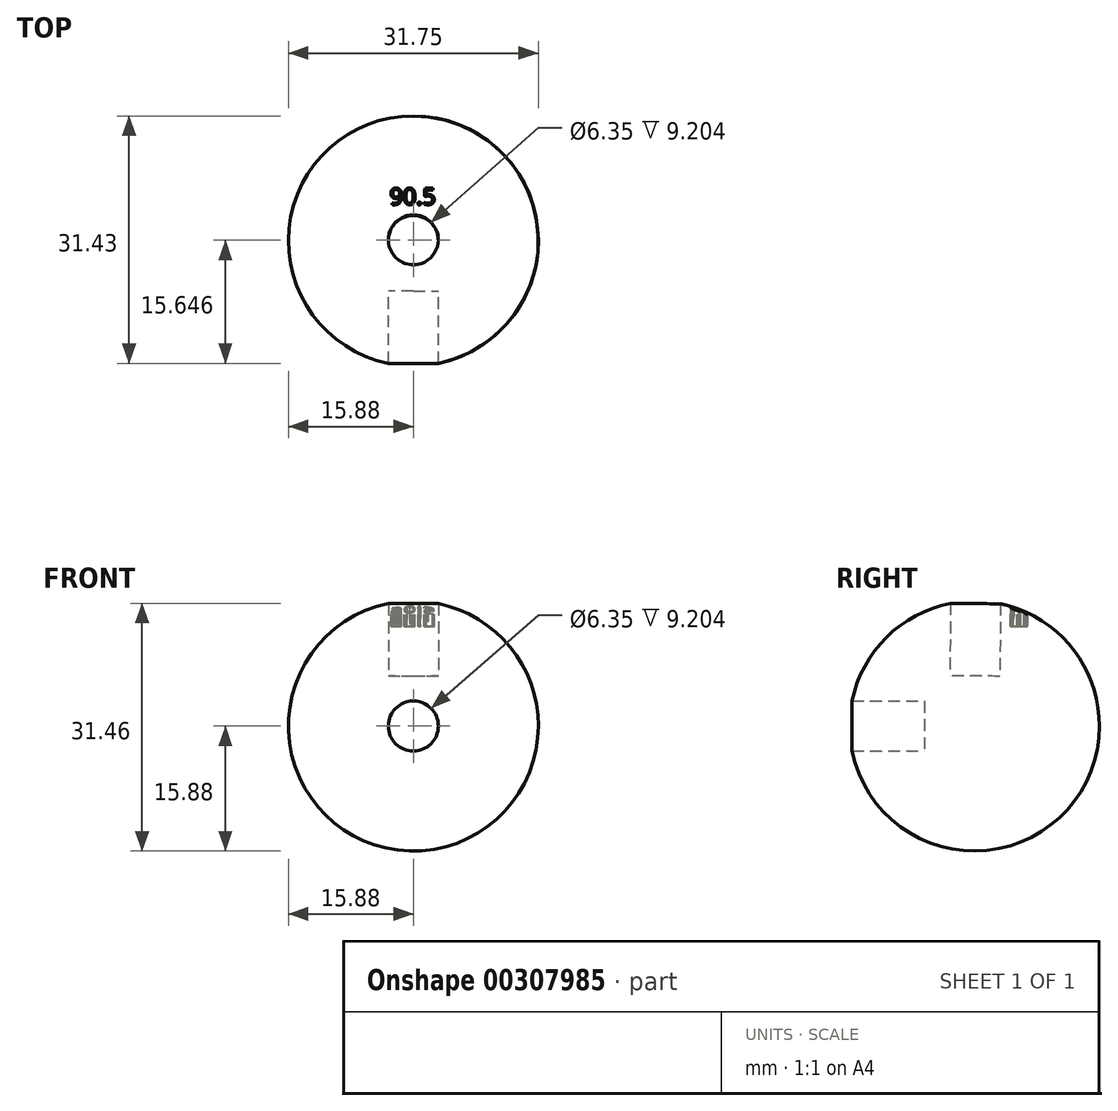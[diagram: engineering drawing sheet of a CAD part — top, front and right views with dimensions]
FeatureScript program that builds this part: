
annotation { "Feature Type Name" : "Feature", "Feature Type Description" : "" }
export const myFeature = defineFeature(function(context is Context, id is Id, definition is map)
    precondition{}
    {
        {
            var Q0;
            Q0=qCreatedBy(makeId("Front.planeOp"),FACE);
            var sketch = newSketch(context, id + "F0", { "sketchPlane" : qUnion([Q0])});
            skCircle(sketch, "E0", {"center": v(0, 0) * mm, "radius": 15.88 * mm});
            skLineSegment(sketch, "E1", {"start": v(0, 0) * mm, "end": v(63.23, 0) * mm, "construction": true});
            skLineSegment(sketch, "E2", {"start": v(0, 0) * mm, "end": v(0, 58.8) * mm, "construction": true});
            skSolve(sketch);
        }
        {
            var Q0;
            Q0=qCreatedBy(makeId("Top.planeOp"),FACE);
            var sketch = newSketch(context, id + "F1", { "sketchPlane" : qUnion([Q0])});
            skArc(sketch, "E3", {"start": v(0, 15.88) * mm, "mid": v(-15.88, 0) * mm, "end": v(0, -15.88) * mm});
            skLineSegment(sketch, "E4", {"start": v(0, 15.88) * mm, "end": v(0, -15.88) * mm});
            skSolve(sketch);
        }
        {
            var Q0;
            Q0=makeQuery(id+"F1.imprint","IMPRINT",FACE,{"disambiguationData":[TD([[makeQuery(id+"F1.imprint","IMPRINT",EDGE,{"derivedFrom":sQuery(id+"F1.wireOp",EDGE,"E3")}),1.0]])]});
            var Q1;
            Q1=sQuery(id+"F0.wireOp",EDGE,"E0");
            revolve(context, id + "F2", {"entities" : qUnion([Q0]), "axis" : qUnion([Q1]), "revolveType" : RevolveType.FULL});
        }
        {
            var Q0;
            Q0=qCreatedBy(makeId("Front.planeOp"),FACE);
            cPlane(context, id + "F3", {"entities" : qUnion([Q0]), "cplaneType" : CPlaneType.OFFSET, "offset" : 6.35 * mm, "width" : 152.4 * mm, "height" : 152.4 * mm});
        }
        {
            var Q0;
            Q0=qCreatedBy(id+"F3.planeOp",FACE);
            var sketch = newSketch(context, id + "F4", { "sketchPlane" : qUnion([Q0])});
            skCircle(sketch, "E5", {"center": v(0, 0) * mm, "radius": 3.18 * mm});
            skSolve(sketch);
        }
        {
            var Q0;
            Q0=qSketchRegion(id+"F4",true);
            extrude(context, id + "F5", {"entities" : qUnion([Q0]), "depth" : 25.4 * mm});
        }
        {
            var Q0;
            Q0=qCreatedBy(makeId("Front.planeOp"),FACE);
            var sketch = newSketch(context, id + "F6", { "sketchPlane" : qUnion([Q0])});
            skLineSegment(sketch, "E6", {"start": v(0, 0) * mm, "end": v(57.52, 0) * mm, "construction": true});
            skSolve(sketch);
        }
        {
            var Q0;
            Q0=makeQuery(id+"F5.opExtrude","SWEPT_BODY",BODY,{"disambiguationData":[OSD([sQuery(id+"F4.wireOp",EDGE,"E5")])]});
            var Q1;
            Q1=sQuery(id+"F6.wireOp",EDGE,"E6");
            transform(context, id + "F7", {"entities" : qUnion([Q0]), "transformType" : TransformType.ROTATION, "transformAxis" : qUnion([Q1]), "angle" : 90.5 * degree, "oppositeDirection" : true, "makeCopy" : true});
        }
        {
            var Q0;
            Q0=makeQuery(id+"F7.opPattern","COPY",FACE,{"derivedFrom":makeQuery(id+"F5.opExtrude","CAP_FACE",FACE,{"disambiguationData":[OSD([sQuery(id+"F4.wireOp",EDGE,"E5")])],"isStart":false}),"instanceName":"1"});
            cPlane(context, id + "F8", {"entities" : qUnion([Q0]), "cplaneType" : CPlaneType.OFFSET, "offset" : 12.7 * mm, "oppositeDirection" : true, "width" : 152.4 * mm, "height" : 152.4 * mm});
        }
        {
            var Q0;
            Q0=qCreatedBy(id+"F8.planeOp",FACE);
            var sketch = newSketch(context, id + "F9", { "sketchPlane" : qUnion([Q0])});
            skText(sketch, "E7", { "text": "90.5", "fontName": "OpenSans-Regular.ttf"});
            const initialGuessF9  = {"E7": [-0.003, 0.00447, 1, 0, 0.00212]};
            skSetInitialGuess(sketch, initialGuessF9);
            skSolve(sketch);
        }
        {
            var Q0;
            Q0 = qSketchRegion(id + "F9", true);
            extrude(context, id + "F10", {"entities" : qUnion([Q0]), "operationType" : NewBodyOperationType.REMOVE, "oppositeDirection" : true, "depth" : 6.35 * mm});
        }
        {
            var Q0;
            Q0=makeQuery(id+"F7.opPattern","COPY",BODY,{"derivedFrom":makeQuery(id+"F5.opExtrude","SWEPT_BODY",BODY,{"disambiguationData":[OSD([sQuery(id+"F4.wireOp",EDGE,"E5")])]}),"instanceName":"1"});
            var Q1;
            Q1=makeQuery(id+"F5.opExtrude","SWEPT_BODY",BODY,{"disambiguationData":[OSD([sQuery(id+"F4.wireOp",EDGE,"E5")])]});
            var Q2;
            Q2=makeQuery(id+"F2.opRevolve","SWEPT_BODY",BODY,{"disambiguationData":[OSD([sQuery(id+"F1.wireOp",EDGE,"E3"),sQuery(id+"F1.wireOp",EDGE,"E4")])]});
            booleanBodies(context, id + "F11", {"operationType" : BooleanOperationType.SUBTRACTION, "tools" : qUnion([Q0, Q1]), "targets" : qUnion([Q2])});
        }
    });
